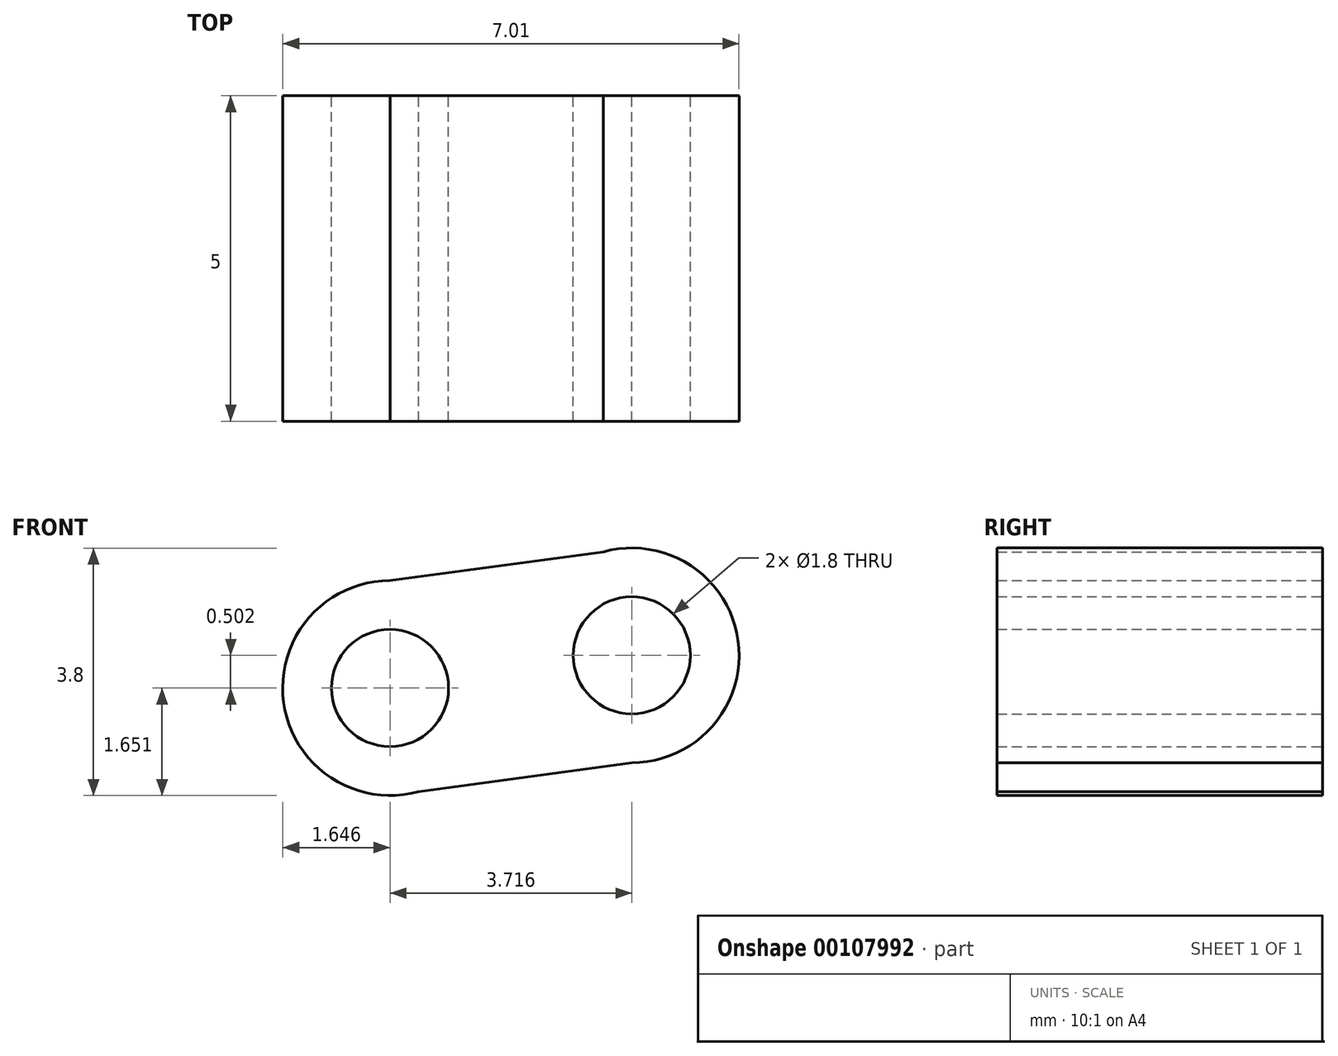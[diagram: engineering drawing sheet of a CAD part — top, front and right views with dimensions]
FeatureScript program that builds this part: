
annotation { "Feature Type Name" : "Feature", "Feature Type Description" : "" }
export const myFeature = defineFeature(function(context is Context, id is Id, definition is map)
    precondition{}
    {
        {
            var Q0;
            Q0=qCreatedBy(makeId("Front.planeOp"),FACE);
            var sketch = newSketch(context, id + "F0", { "sketchPlane" : qUnion([Q0])});
            skCircle(sketch, "E0", {"center": v(-47.71, 36.2) * mm, "radius": 0.9 * mm});
            skCircle(sketch, "E1", {"center": v(-47.71, 36.2) * mm, "radius": 1.65 * mm});
            skCircle(sketch, "E2", {"center": v(-44, 36.7) * mm, "radius": 0.9 * mm});
            skCircle(sketch, "E3", {"center": v(-44, 36.7) * mm, "radius": 1.65 * mm});
            skLineSegment(sketch, "E4", {"start": v(-47.71, 37.84) * mm, "end": v(-44, 38.34) * mm});
            skLineSegment(sketch, "E5", {"start": v(-47.71, 34.54) * mm, "end": v(-44, 35.04) * mm});
            skSolve(sketch);
        }
        {
            var Q0;
            Q0 = qSketchRegion(id + "F0", true);
            extrude(context, id + "F1", {"entities" : qUnion([Q0]), "depth" : 5 * mm});
        }
    });
